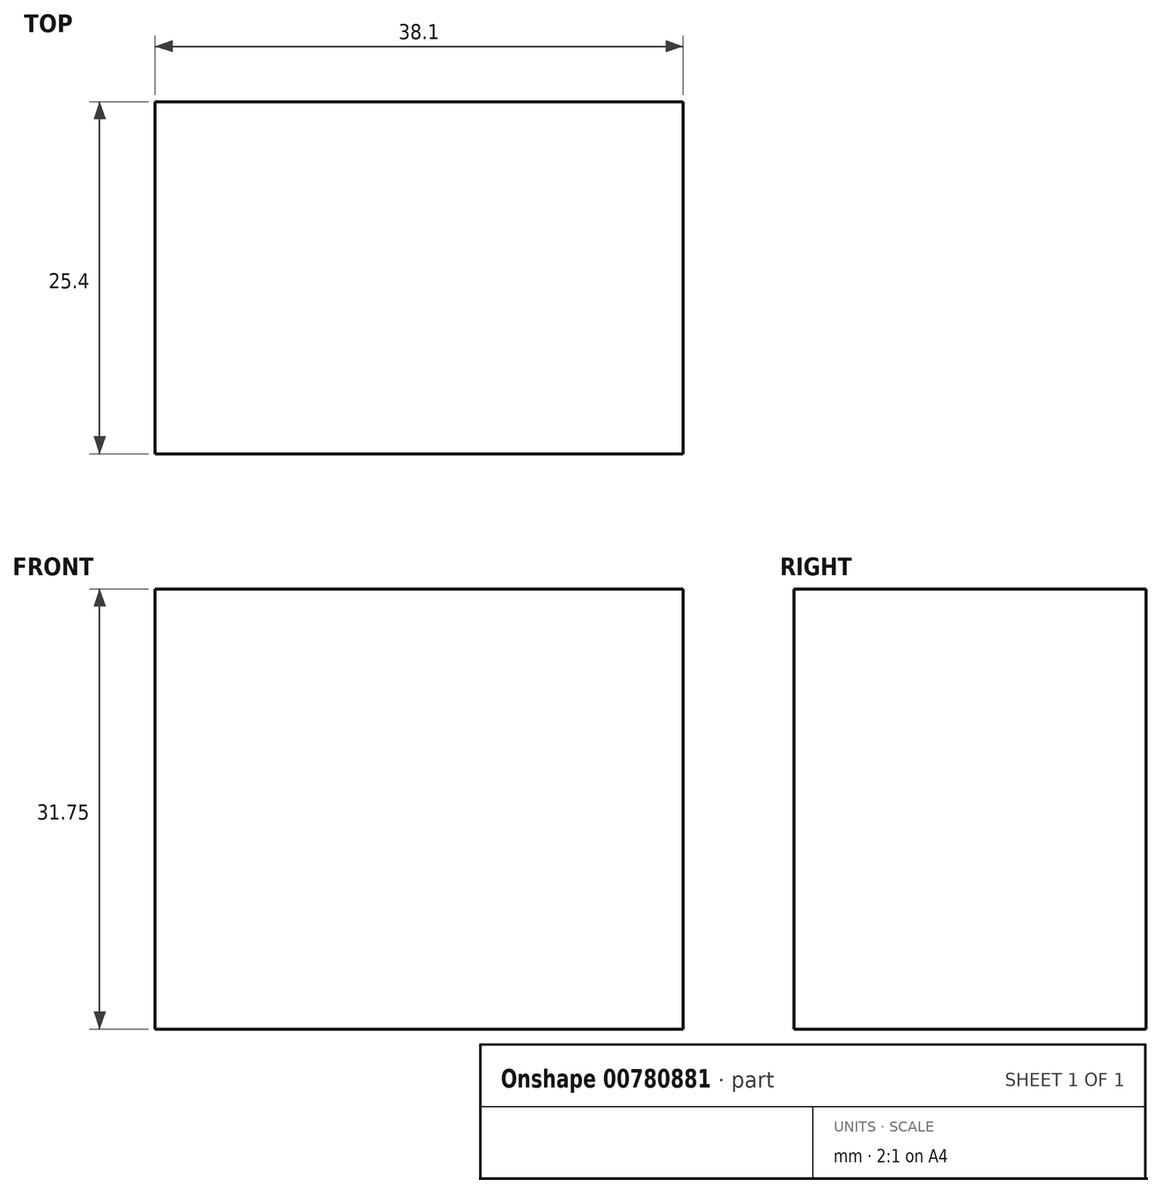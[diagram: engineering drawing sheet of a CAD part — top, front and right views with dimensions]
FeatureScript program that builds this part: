
annotation { "Feature Type Name" : "Feature", "Feature Type Description" : "" }
export const myFeature = defineFeature(function(context is Context, id is Id, definition is map)
    precondition{}
    {
        {
            var Q0;
            Q0=qCreatedBy(makeId("Front.planeOp"),FACE);
            var sketch = newSketch(context, id + "F0", { "sketchPlane" : qUnion([Q0])});
            skLineSegment(sketch, "E0", {"start": v(0, 0) * mm, "end": v(38.1, 0) * mm});
            skLineSegment(sketch, "E1", {"start": v(38.1, 0) * mm, "end": v(38.1, 31.75) * mm});
            skLineSegment(sketch, "E2", {"start": v(41.71, 31.75) * mm, "end": v(0, 31.75) * mm});
            skLineSegment(sketch, "E3", {"start": v(0, 31.75) * mm, "end": v(0, 0) * mm});
            skSolve(sketch);
        }
        {
            var Q0;
            Q0 = qSketchRegion(id + "F0", true);
            extrude(context, id + "F1", {"entities" : qUnion([Q0]), "depth" : 25.4 * mm, "offsetDistance" : 25.4 * mm});
        }
    });
